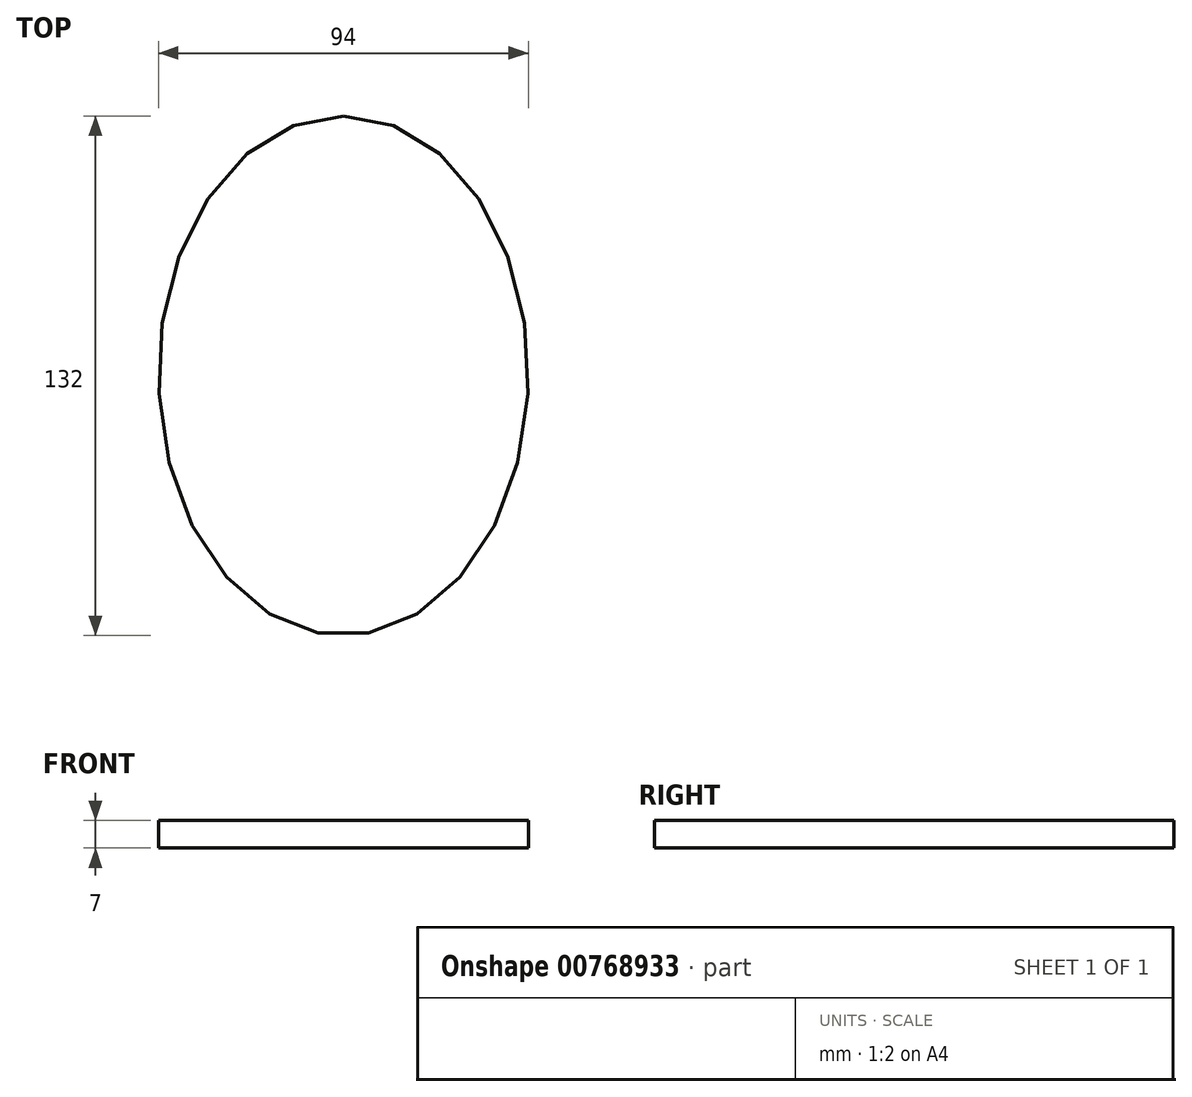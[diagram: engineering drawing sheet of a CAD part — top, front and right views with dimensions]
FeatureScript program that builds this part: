
annotation { "Feature Type Name" : "Feature", "Feature Type Description" : "" }
export const myFeature = defineFeature(function(context is Context, id is Id, definition is map)
    precondition{}
    {
        {
            var Q0;
            Q0=qCreatedBy(makeId("Top.planeOp"),FACE);
            var sketch = newSketch(context, id + "F0", { "sketchPlane" : qUnion([Q0])});
            skLineSegment(sketch, "E0", {"start": v(0, 66) * mm, "end": v(0, -66) * mm, "construction": true});
            skLineSegment(sketch, "E1", {"start": v(47, 0) * mm, "end": v(-47, 0) * mm, "construction": true});
            skEllipse(sketch, "E2", {"center": v(0, 0) * mm, "majorRadius": 66 * mm, "minorRadius": 47 * mm, "majorAxis": v(0, 1)});
            skSolve(sketch);
        }
        {
            var Q0;
            Q0 = qSketchRegion(id + "F0", true);
            extrude(context, id + "F1", {"entities" : qUnion([Q0]), "depth" : 7 * mm, "offsetDistance" : 25 * mm});
        }
    });
